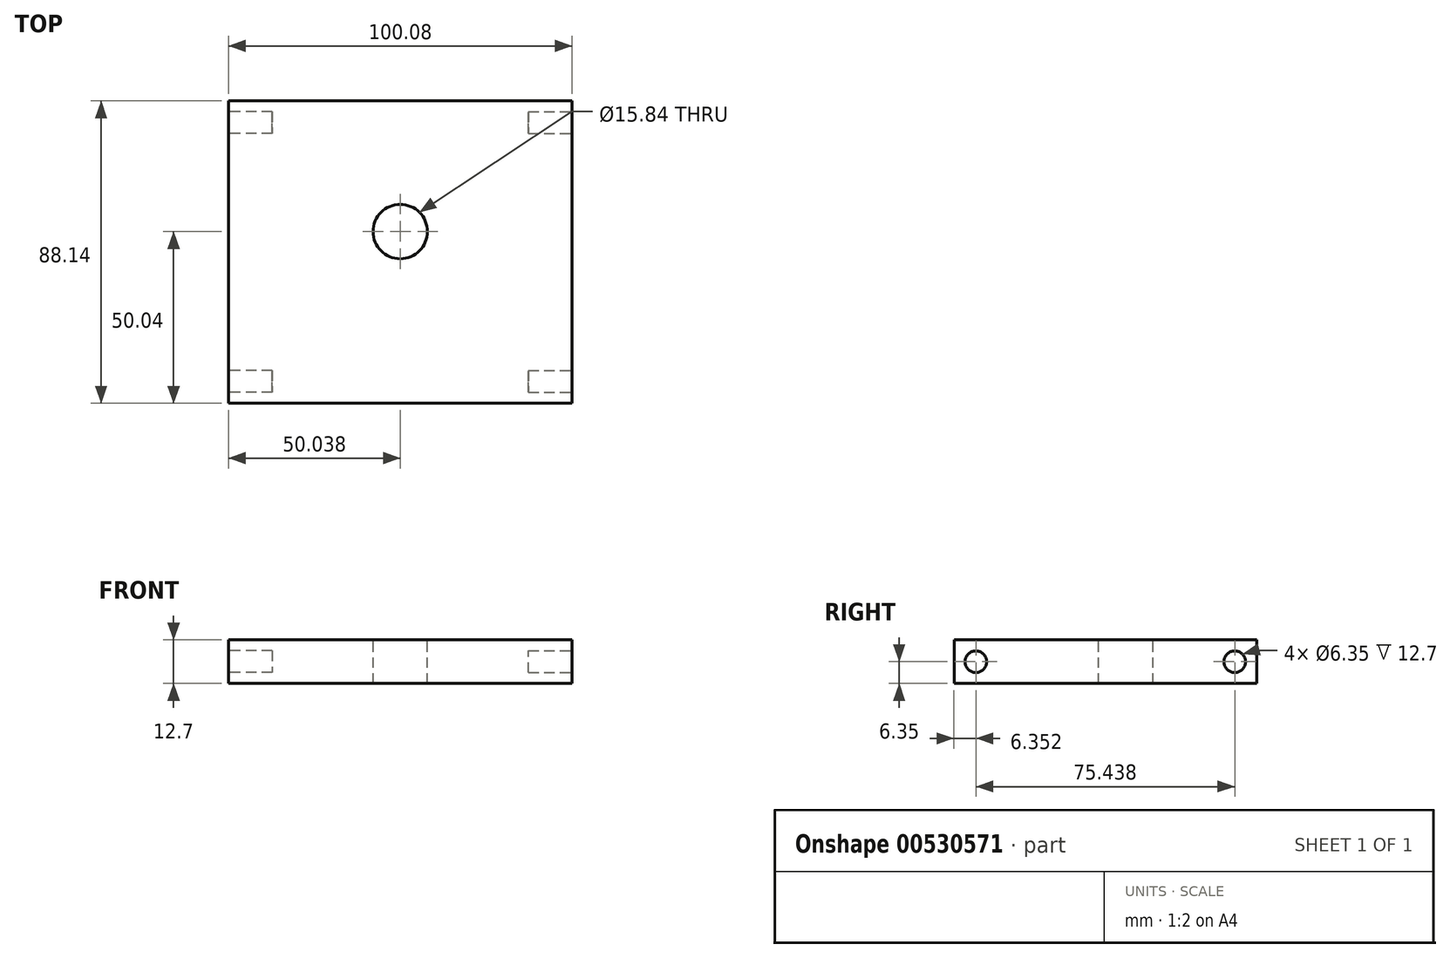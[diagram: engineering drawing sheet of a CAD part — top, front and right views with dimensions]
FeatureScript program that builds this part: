
annotation { "Feature Type Name" : "Feature", "Feature Type Description" : "" }
export const myFeature = defineFeature(function(context is Context, id is Id, definition is map)
    precondition{}
    {
        {
            var Q0;
            Q0=qCreatedBy(makeId("Top.planeOp"),FACE);
            var sketch = newSketch(context, id + "F0", { "sketchPlane" : qUnion([Q0])});
            skLineSegment(sketch, "E0.bottom", {"start": v(0, 0) * mm, "end": v(100.08, 0) * mm});
            skLineSegment(sketch, "E0.top", {"start": v(0, -88.14) * mm, "end": v(100.08, -88.14) * mm});
            skLineSegment(sketch, "E0.left", {"start": v(0, 0) * mm, "end": v(0, -88.14) * mm});
            skLineSegment(sketch, "E0.right", {"start": v(100.08, 0) * mm, "end": v(100.08, -88.14) * mm});
            skSolve(sketch);
        }
        {
            var Q0;
            Q0 = qSketchRegion(id + "F0", true);
            extrude(context, id + "F1", {"entities" : qUnion([Q0]), "depth" : 12.7 * mm, "offsetDistance" : 25.4 * mm});
        }
        {
            var Q0;
            Q0=makeQuery(id+"F1.opExtrude","CAP_FACE",FACE,{"disambiguationData":[OSD([sQuery(id+"F0.wireOp",EDGE,"E0.bottom"),sQuery(id+"F0.wireOp",EDGE,"E0.top"),sQuery(id+"F0.wireOp",EDGE,"E0.left"),sQuery(id+"F0.wireOp",EDGE,"E0.right")])],"isStart":false});
            var sketch = newSketch(context, id + "F2", { "sketchPlane" : qUnion([Q0])});
            skCircle(sketch, "E1", {"center": v(50.04, -38.1) * mm, "radius": 7.92 * mm});
            skSolve(sketch);
        }
        {
            var Q0;
            Q0 = qSketchRegion(id + "F2", true);
            extrude(context, id + "F3", {"entities" : qUnion([Q0]), "operationType" : NewBodyOperationType.REMOVE, "endBound" : BoundingType.THROUGH_ALL, "oppositeDirection" : true, "depth" : 25.4 * mm, "offsetDistance" : 25.4 * mm});
        }
        {
            var Q0;
            Q0=makeQuery(id+"F1.opExtrude","SWEPT_FACE",FACE,{"disambiguationData":[OSD([sQuery(id+"F0.wireOp",EDGE,"E0.right")])]});
            var sketch = newSketch(context, id + "F4", { "sketchPlane" : qUnion([Q0])});
            skCircle(sketch, "E2", {"center": v(-81.79, 6.35) * mm, "radius": 3.18 * mm});
            skCircle(sketch, "E3", {"center": v(-6.35, 6.35) * mm, "radius": 3.18 * mm});
            skSolve(sketch);
        }
        {
            var Q0;
            Q0 = qSketchRegion(id + "F4", true);
            extrude(context, id + "F5", {"entities" : qUnion([Q0]), "operationType" : NewBodyOperationType.REMOVE, "oppositeDirection" : true, "depth" : 12.7 * mm, "offsetDistance" : 25.4 * mm});
        }
        {
            var Q0;
            Q0=makeQuery(id+"F1.opExtrude","SWEPT_FACE",FACE,{"disambiguationData":[OSD([sQuery(id+"F0.wireOp",EDGE,"E0.left")])]});
            var sketch = newSketch(context, id + "F6", { "sketchPlane" : qUnion([Q0])});
            skCircle(sketch, "E4", {"center": v(6.35, 6.35) * mm, "radius": 3.18 * mm});
            skCircle(sketch, "E5", {"center": v(81.79, 6.35) * mm, "radius": 3.18 * mm});
            skSolve(sketch);
        }
        {
            var Q0;
            Q0 = qSketchRegion(id + "F6", true);
            extrude(context, id + "F7", {"entities" : qUnion([Q0]), "operationType" : NewBodyOperationType.REMOVE, "oppositeDirection" : true, "depth" : 12.7 * mm, "offsetDistance" : 25.4 * mm});
        }
    });
